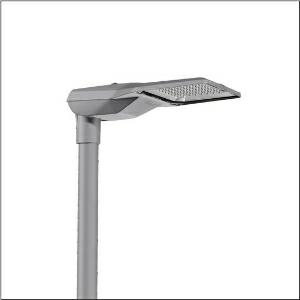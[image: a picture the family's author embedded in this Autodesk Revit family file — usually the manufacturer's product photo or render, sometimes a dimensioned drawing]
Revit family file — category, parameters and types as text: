
# Revit family: streetlight_sl_21_midi___st0_8a_5xe3c33s08lb_6676
name_source: partatom
category: Lighting Fixtures
units: mm (PartAtom-declared; Revit-internal decimal feet)

## family parameters
Cut with Voids When Loaded = No
Host = Face
Light Source = No
Part Type = Normal
Room Calculation Point = No
Round Connector Dimension = Use Diameter
Shared = No

## types (1)
- --- (1 x LED, 14340 lm, 99.6 W, 3000K)
    Apparent Load = 100 VA
    CIE Flux Codes = 38 75 97 100 100
    Color Rendering = 70
    Color Temperature = 3000K
    Default Elevation = 1800 mm
    Description = Streetlight SL 21 midi, mast luminaire, primary light control with lens, of PMMA, primary optical cover: cover, of toughened safety glass, transparent, light distribution: ST0.8a, light emission: direct distribution, primary light characteristic: asymmetric, installation type: side-entry, post-top, LED, High Power LED, rated luminous flux: 14.340lm, luminous efficacy: 144lm/W, light colour: 730, colour temperature: 3000K, control gear: D4i, control: overheat protection, constant luminous flux control, time-dependent luminous flux control, flexible luminous flux parameterisation, pre-setting: logarithmic dimming characteristic, mains connection: 230..240V, AC, 50/60Hz, start of lifetime: 100W, end of service life: 102W, reduction: 46W, luminaire housing, of diecast aluminium, powder-coated, SITECO metallic grey (DB 702S), corrosivity category C5 high according to DIN EN ISO 12944, please order mast flange separately, inclination adjustable: 0°, 5°, 10°, 15°, sealing non-destructively replaceable, multi-level sealing system, length: 644mm, width: 335mm, height: 110mm, mast flange for spigot size: 42mm (side-entry): 5XC10008XM4, 60/48mm (side-entry/post-top): 5XC10108XM2, 76/60mm (side-entry/post-top): 5XC10108XM1, mounting height: 4..8m, Smart Interface above, protection rating (complete): IP66, insulation class (complete): insulation class II (safety insulation), certification: CE, ENEC, ENEC+, VDE, impact resistance: IK10, permissible operating ambient temperature for outdoor applications: -40..+50°C, standard-compliant lighting for roads and squares, packaging unit: 1 piece

Light Distribution: ST0.8a
    Height = 111 mm
    Lamp = 1 x LED
    Lamp Light Flux = 14340 lm
    Lamp Power = 99.6 W
    Lamp count = 1
    Length = 644 mm
    Luminous efficacy = 144 lm/W
    Manufacturer = Siteco
    ModVariant = No
    Model = 5XE3C33S08LB
    Number of Poles = 1
    OnlyDefault = Yes
    Power Factor = 1
    Product Name = Streetlight SL 21 midi | ST0.8a
    Product group = mast luminaire | pylon top
    ProductGroupID = 6100
    Protection Class = Protection class II
    Protection Degree = IP 66
    RLX_Detail_Level = 1
    RLX_Emergency_Light_Flux = 0 lm
    RLX_Emergency_Type = 0
    RLX_Emergency_Type_DB = No
    RlxData = <blob elided: 26861 chars, md5=404d72c7>
    Socket = socket
    Standby Power = 0 W
    System Light Flux = 14340 lm
    System Power = 100 W
    Type Comments = factory setting: luminous flux: 100 % | dim-lin: 254 | 1020 mA
    Type Image = l_1004302.jpg
    URL = http://relux.com
    VarID = @adj_030893
    Voltage = 0 V
    Weight = 0.00 kg
    Width = 336 mm

## geometry (parser evidence)
native form markers: Blend x4, Sweep x11
no freeform markers — native parametric forms only
